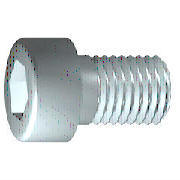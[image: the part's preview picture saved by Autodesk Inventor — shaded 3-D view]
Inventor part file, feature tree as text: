
AUTODESK INVENTOR PART (.ipt)
format: ipt  version: 2017 (Build 210142000, 142)  size: 185,856 bytes
history: native  units: mm (DEFAULTED — no unit token found)
features: sketch x2, extrude x1, plane x1, fillet x1
ambient origin geometry x7: Origin, YZ Plane, XY Plane, X Axis, Y Axis, Z Axis, Center Point
bodies: Solid1 (feature_tree), Body (feature_tree)
feature tree (5):
  extrude  "Slot"  Depth=3.0mm
  plane  "Work Plane1"
  fillet  "Fillet2"  Radius=3.0mm
  sketch  "Sketch1"  dims[d1=19.08655mm d2=0.306825mm d3=3.0mm]
  sketch  "Sketch2"  dims[d4=1.5mm d5=60.0deg d6=3.0mm d7=3.0mm d8=2.886751mm d9=5.5mm d10=90.0deg d11=10.0mm d12=0.0mm d13=19.08655mm d14=0.0mm d15=0.306725mm d16=0.306725mm d17=0.3mm d19=0.0mm d26=20.0mm d27=45.0deg d28=0.0mm d29=0.0mm d30=0.1mm]
